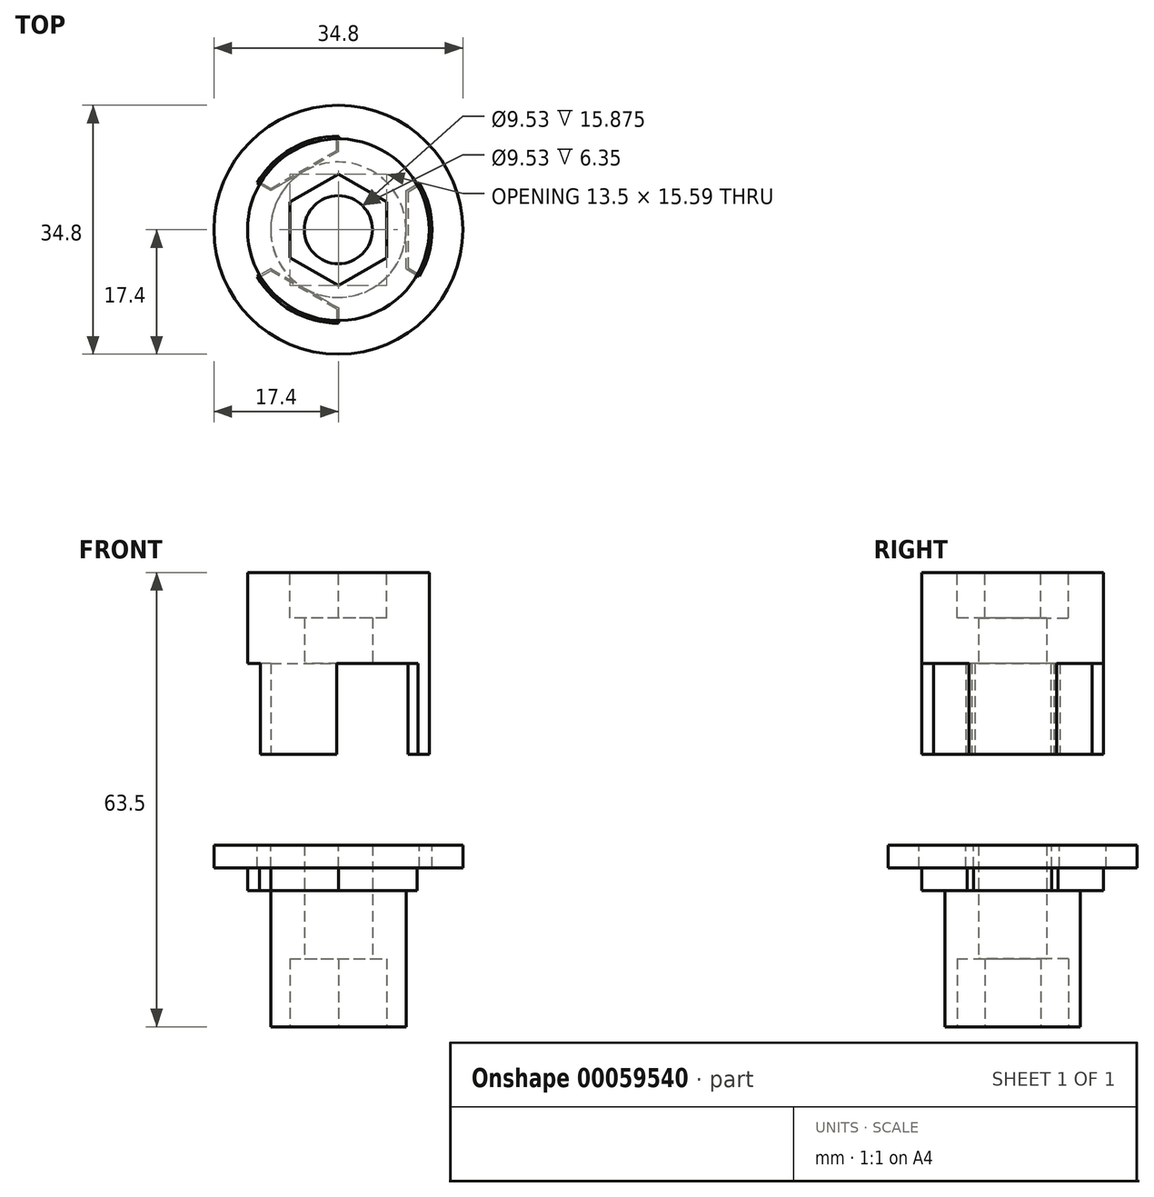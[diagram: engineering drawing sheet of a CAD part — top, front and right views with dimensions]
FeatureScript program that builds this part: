
annotation { "Feature Type Name" : "Feature", "Feature Type Description" : "" }
export const myFeature = defineFeature(function(context is Context, id is Id, definition is map)
    precondition{}
    {
        {
            var Q0;
            Q0=qCreatedBy(makeId("Front.planeOp"),FACE);
            var sketch = newSketch(context, id + "F0", { "sketchPlane" : qUnion([Q0])});
            skLineSegment(sketch, "E0", {"start": v(0, 0) * mm, "end": v(0, 20.45) * mm, "construction": true});
            skLineSegment(sketch, "E1", {"start": v(-4.76, 0) * mm, "end": v(-4.76, 6.35) * mm});
            skLineSegment(sketch, "E2", {"start": v(-4.76, 6.35) * mm, "end": v(-4.76, 6.35) * mm});
            skLineSegment(sketch, "E3", {"start": v(-4.76, 6.35) * mm, "end": v(-4.76, 25.4) * mm});
            skLineSegment(sketch, "E4", {"start": v(-4.76, 25.4) * mm, "end": v(-12.7, 25.4) * mm});
            skLineSegment(sketch, "E5", {"start": v(-12.7, 25.4) * mm, "end": v(-12.7, 19.05) * mm});
            skLineSegment(sketch, "E6", {"start": v(-12.7, 19.05) * mm, "end": v(-9.46, 19.05) * mm});
            skLineSegment(sketch, "E7", {"start": v(-9.46, 19.05) * mm, "end": v(-9.46, 0) * mm});
            skLineSegment(sketch, "E8", {"start": v(-9.46, 0) * mm, "end": v(-4.76, 0) * mm});
            skSolve(sketch);
        }
        {
            var Q0;
            Q0=makeQuery(id+"F0.imprint","IMPRINT",FACE,{"disambiguationData":[TD([[makeQuery(id+"F0.imprint","IMPRINT",EDGE,{"derivedFrom":sQuery(id+"F0.wireOp",EDGE,"E1")}),1.0]])]});
            var Q1;
            Q1=sQuery(id+"F0.wireOp",EDGE,"E0");
            revolve(context, id + "F1", {"entities" : qUnion([Q0]), "axis" : qUnion([Q1]), "revolveType" : RevolveType.FULL});
        }
        {
            var Q0;
            Q0=makeQuery(id+"F1.opRevolve","SWEPT_FACE",FACE,{"disambiguationData":[OSD([sQuery(id+"F0.wireOp",EDGE,"E8")])]});
            var sketch = newSketch(context, id + "F2", { "sketchPlane" : qUnion([Q0])});
            skCircle(sketch, "E9.cCircle", {"center": v(0, 0) * mm, "radius": 6.75 * mm, "construction": true});
            skLineSegment(sketch, "E9.0", {"start": v(6.75, 3.9) * mm, "end": v(6.75, -3.9) * mm});
            skLineSegment(sketch, "E9.1", {"start": v(6.75, -3.9) * mm, "end": v(0, -7.8) * mm});
            skLineSegment(sketch, "E9.2", {"start": v(0, -7.8) * mm, "end": v(-6.75, -3.9) * mm});
            skLineSegment(sketch, "E9.3", {"start": v(-6.75, -3.9) * mm, "end": v(-6.75, 3.9) * mm});
            skLineSegment(sketch, "E9.4", {"start": v(-6.75, 3.9) * mm, "end": v(0, 7.8) * mm});
            skLineSegment(sketch, "E9.5", {"start": v(0, 7.8) * mm, "end": v(6.75, 3.9) * mm});
            skPoint(sketch, "E9.0.midPoint", {"position": v(6.75, 0) * mm});
            skSolve(sketch);
        }
        {
            var Q0;
            Q0=makeQuery(id+"F2.imprint","IMPRINT",FACE,{"disambiguationData":[TD([[makeQuery(id+"F2.imprint","IMPRINT",EDGE,{"derivedFrom":sQuery(id+"F2.wireOp",EDGE,"E9.0")}),-1.0]])]});
            var Q1;
            Q1=makeQuery(id+"F1.opRevolve","SWEPT_FACE",FACE,{"disambiguationData":[OSD([sQuery(id+"F0.wireOp",EDGE,"E2")])]});
            extrude(context, id + "F3", {"entities" : qUnion([Q0]), "operationType" : NewBodyOperationType.REMOVE, "oppositeDirection" : true, "endBoundEntityFace" : qUnion([Q1]), "depth" : 9.52 * mm});
        }
        {
            var Q0;
            Q0=makeQuery(id+"F1.opRevolve","SWEPT_FACE",FACE,{"disambiguationData":[OSD([sQuery(id+"F0.wireOp",EDGE,"E4")])]});
            var sketch = newSketch(context, id + "F4", { "sketchPlane" : qUnion([Q0])});
            skLineSegment(sketch, "E10", {"start": v(0, 10.93) * mm, "end": v(0, 12.7) * mm});
            skLineSegment(sketch, "E11", {"start": v(0, 12.7) * mm, "end": v(-7.33, 12.7) * mm});
            skPoint(sketch, "E12.center", {"position": v(0, 0) * mm});
            skLineSegment(sketch, "E13", {"start": v(0, 0) * mm, "end": v(-7.33, 12.7) * mm, "construction": true});
            skLineSegment(sketch, "E14.MirrorCS", {"start": v(-11, 6.35) * mm, "end": v(-7.33, 12.7) * mm});
            skLineSegment(sketch, "E15.MirrorCS", {"start": v(-9.46, 5.46) * mm, "end": v(-11, 6.35) * mm});
            skLineSegment(sketch, "E16", {"start": v(0, 10.93) * mm, "end": v(-4.73, 8.2) * mm});
            skLineSegment(sketch, "E17.MirrorCS", {"start": v(-9.46, 16.39) * mm, "end": v(-2.13, 3.69) * mm, "construction": true});
            skLineSegment(sketch, "E18.MirrorCS", {"start": v(-9.46, 5.46) * mm, "end": v(-4.73, 8.2) * mm});
            skLineSegment(sketch, "E19.1.0", {"start": v(-9.46, -5.46) * mm, "end": v(-4.73, -8.2) * mm});
            skLineSegment(sketch, "E19.1.1", {"start": v(-11, -6.35) * mm, "end": v(-7.33, -12.7) * mm});
            skLineSegment(sketch, "E19.1.2", {"start": v(-9.46, -16.39) * mm, "end": v(-2.13, -3.69) * mm, "construction": true});
            skLineSegment(sketch, "E19.1.3", {"start": v(0, -10.93) * mm, "end": v(-4.73, -8.2) * mm});
            skLineSegment(sketch, "E19.1.4", {"start": v(0, -12.7) * mm, "end": v(-7.33, -12.7) * mm});
            skLineSegment(sketch, "E19.1.5", {"start": v(-9.46, -5.46) * mm, "end": v(-11, -6.35) * mm});
            skLineSegment(sketch, "E19.1.6", {"start": v(0, 0) * mm, "end": v(-7.33, -12.7) * mm, "construction": true});
            skLineSegment(sketch, "E19.1.7", {"start": v(0, -10.93) * mm, "end": v(0, -12.7) * mm});
            skLineSegment(sketch, "E19.2.0", {"start": v(9.46, -5.46) * mm, "end": v(9.46, 0) * mm});
            skLineSegment(sketch, "E19.2.1", {"start": v(11, -6.35) * mm, "end": v(14.66, 0) * mm});
            skLineSegment(sketch, "E19.2.2", {"start": v(18.92, 0) * mm, "end": v(4.26, 0) * mm, "construction": true});
            skLineSegment(sketch, "E19.2.3", {"start": v(9.46, 5.46) * mm, "end": v(9.46, 0) * mm});
            skLineSegment(sketch, "E19.2.4", {"start": v(11, 6.35) * mm, "end": v(14.66, 0) * mm});
            skLineSegment(sketch, "E19.2.5", {"start": v(9.46, -5.46) * mm, "end": v(11, -6.35) * mm});
            skLineSegment(sketch, "E19.2.6", {"start": v(0, 0) * mm, "end": v(14.66, 0) * mm, "construction": true});
            skLineSegment(sketch, "E19.2.7", {"start": v(9.46, 5.46) * mm, "end": v(11, 6.35) * mm});
            skSolve(sketch);
        }
        {
            var Q0;
            {var subQ1=sQuery(id+"F4.wireOp",EDGE,"E10");Q0=makeQuery(id+"F4.imprint","IMPRINT",FACE,{"disambiguationData":[TD([[makeQuery(id+"F4.imprint","IMPRINT",EDGE,{"derivedFrom":subQ1}),1.0]])]});}
            var Q1;
            Q1=makeQuery(id+"F4.imprint","IMPRINT",FACE,{"disambiguationData":[TD([[makeQuery(id+"F4.imprint","IMPRINT",EDGE,{"derivedFrom":sQuery(id+"F4.wireOp",EDGE,"E19.1.0")}),-1.0]])]});
            var Q2;
            Q2=makeQuery(id+"F4.imprint","IMPRINT",FACE,{"disambiguationData":[TD([[makeQuery(id+"F4.imprint","IMPRINT",EDGE,{"derivedFrom":sQuery(id+"F4.wireOp",EDGE,"E19.2.0")}),-1.0]])]});
            extrude(context, id + "F5", {"entities" : qUnion([Q0, Q1, Q2]), "operationType" : NewBodyOperationType.REMOVE, "oppositeDirection" : true, "depth" : 25.4 * mm});
        }
        {
            var Q0;
            Q0=makeQuery(id+"F1.opRevolve","SWEPT_FACE",FACE,{"disambiguationData":[OSD([sQuery(id+"F0.wireOp",EDGE,"E4")])]});
            cPlane(context, id + "F6", {"entities" : qUnion([Q0]), "cplaneType" : CPlaneType.OFFSET, "offset" : 12.7 * mm, "width" : 152.4 * mm, "height" : 152.4 * mm});
        }
        {
            var Q0;
            Q0=qCreatedBy(id+"F6.planeOp",FACE);
            var sketch = newSketch(context, id + "F7", { "sketchPlane" : qUnion([Q0])});
            skLineSegment(sketch, "E20.0", {"start": v(0, 11) * mm, "end": v(0, 12.7) * mm, "construction": true});
            skLineSegment(sketch, "E21.0", {"start": v(-0.25, 11.07) * mm, "end": v(-0.25, 12.7) * mm});
            skLineSegment(sketch, "E21.1", {"start": v(-9.46, 5.76) * mm, "end": v(-0.25, 11.07) * mm});
            skLineSegment(sketch, "E21.2", {"start": v(-9.46, 5.76) * mm, "end": v(-10.87, 6.57) * mm});
            skArc(sketch, "E22", {"start": v(-0.25, 12.7) * mm, "mid": v(-6.35, 11) * mm, "end": v(-10.87, 6.57) * mm});
            skLineSegment(sketch, "E23.0", {"start": v(-9.46, 5.46) * mm, "end": v(-11, 6.35) * mm, "construction": true});
            skLineSegment(sketch, "E24.0", {"start": v(0, 10.93) * mm, "end": v(-9.46, 5.46) * mm, "construction": true});
            skLineSegment(sketch, "E25.1.0", {"start": v(-9.46, -5.46) * mm, "end": v(0, -10.93) * mm, "construction": true});
            skLineSegment(sketch, "E25.1.1", {"start": v(-0.25, -11.07) * mm, "end": v(-0.25, -12.7) * mm});
            skLineSegment(sketch, "E25.1.2", {"start": v(-9.53, -5.5) * mm, "end": v(-11, -6.35) * mm, "construction": true});
            skLineSegment(sketch, "E25.1.3", {"start": v(0, -10.93) * mm, "end": v(0, -12.7) * mm, "construction": true});
            skLineSegment(sketch, "E25.1.4", {"start": v(-9.46, -5.76) * mm, "end": v(-10.87, -6.57) * mm});
            skLineSegment(sketch, "E25.1.5", {"start": v(-0.25, -11.07) * mm, "end": v(-9.46, -5.76) * mm});
            skArc(sketch, "E25.1.6", {"start": v(-10.87, -6.57) * mm, "mid": v(-6.35, -11) * mm, "end": v(-0.25, -12.7) * mm});
            skLineSegment(sketch, "E25.2.0", {"start": v(9.46, -5.46) * mm, "end": v(9.46, 5.46) * mm, "construction": true});
            skLineSegment(sketch, "E25.2.1", {"start": v(9.72, 5.32) * mm, "end": v(11.12, 6.13) * mm});
            skLineSegment(sketch, "E25.2.2", {"start": v(9.53, -5.5) * mm, "end": v(11, -6.35) * mm, "construction": true});
            skLineSegment(sketch, "E25.2.3", {"start": v(9.46, 5.46) * mm, "end": v(11, 6.35) * mm, "construction": true});
            skLineSegment(sketch, "E25.2.4", {"start": v(9.72, -5.32) * mm, "end": v(11.12, -6.13) * mm});
            skLineSegment(sketch, "E25.2.5", {"start": v(9.72, 5.32) * mm, "end": v(9.72, -5.32) * mm});
            skArc(sketch, "E25.2.6", {"start": v(11.12, -6.13) * mm, "mid": v(12.7, 0) * mm, "end": v(11.12, 6.13) * mm});
            skSolve(sketch);
        }
        {
            var Q0;
            Q0=makeQuery(id+"F7.imprint","IMPRINT",FACE,{"disambiguationData":[TD([[makeQuery(id+"F7.imprint","IMPRINT",EDGE,{"derivedFrom":sQuery(id+"F7.wireOp",EDGE,"E21.0")}),1.0]])]});
            var Q1;
            Q1=makeQuery(id+"F7.imprint","IMPRINT",FACE,{"disambiguationData":[TD([[makeQuery(id+"F7.imprint","IMPRINT",EDGE,{"derivedFrom":sQuery(id+"F7.wireOp",EDGE,"E25.2.1")}),-1.0]])]});
            var Q2;
            Q2=makeQuery(id+"F7.imprint","IMPRINT",FACE,{"disambiguationData":[TD([[makeQuery(id+"F7.imprint","IMPRINT",EDGE,{"derivedFrom":sQuery(id+"F7.wireOp",EDGE,"E25.1.1")}),-1.0]])]});
            extrude(context, id + "F8", {"entities" : qUnion([Q0, Q1, Q2]), "depth" : 12.7 * mm});
        }
        {
            var Q0;
            Q0=makeQuery(id+"F8.opExtrude","CAP_FACE",FACE,{"disambiguationData":[OSD([sQuery(id+"F7.wireOp",EDGE,"E21.0"),sQuery(id+"F7.wireOp",EDGE,"E21.1"),sQuery(id+"F7.wireOp",EDGE,"E21.2"),sQuery(id+"F7.wireOp",EDGE,"E22")])],"isStart":false});
            var sketch = newSketch(context, id + "F9", { "sketchPlane" : qUnion([Q0])});
            skCircle(sketch, "E26", {"center": v(0, 0) * mm, "radius": 12.7 * mm});
            skCircle(sketch, "E27.0", {"center": v(0, 0) * mm, "radius": 4.76 * mm});
            skSolve(sketch);
        }
        {
            var Q0;
            Q0=makeQuery(id+"F9.imprint","IMPRINT",FACE,{"disambiguationData":[TD([[makeQuery(id+"F9.imprint","IMPRINT",EDGE,{"derivedFrom":sQuery(id+"F9.wireOp",EDGE,"E27.0")}),-1.0]])]});
            var Q1;
            {var subQ1=makeQuery(id+"F8.opExtrude","CAP_EDGE",EDGE,{"disambiguationData":[OSD([sQuery(id+"F7.wireOp",EDGE,"E21.0")])],"isStart":false});Q1=makeQuery(id+"F9.imprint","IMPRINT",FACE,{"disambiguationData":[TD([[makeQuery(id+"F9.imprint","IMPRINT",EDGE,{"derivedFrom":subQ1}),1.0]])]});}
            extrude(context, id + "F10", {"entities" : qUnion([Q0, Q1]), "operationType" : NewBodyOperationType.ADD, "depth" : 12.7 * mm});
        }
        {
            var Q0;
            Q0=makeQuery(id+"F10.opExtrude","CAP_FACE",FACE,{"disambiguationData":[OSD([sQuery(id+"F9.wireOp",EDGE,"E26"),sQuery(id+"F9.wireOp",EDGE,"965c656a-fdfc-4771-a508-4816ac5dd99b")])],"isStart":false});
            var sketch = newSketch(context, id + "F11", { "sketchPlane" : qUnion([Q0])});
            skLineSegment(sketch, "E28.0", {"start": v(0, 7.8) * mm, "end": v(-6.75, 3.9) * mm});
            skLineSegment(sketch, "E29.0", {"start": v(6.75, 3.9) * mm, "end": v(0, 7.8) * mm});
            skLineSegment(sketch, "E30.0", {"start": v(6.75, -3.9) * mm, "end": v(6.75, 3.9) * mm});
            skLineSegment(sketch, "E31.0", {"start": v(0, -7.8) * mm, "end": v(6.75, -3.9) * mm});
            skLineSegment(sketch, "E32.0", {"start": v(-6.75, -3.9) * mm, "end": v(0, -7.8) * mm});
            skLineSegment(sketch, "E33.0", {"start": v(-6.75, 3.9) * mm, "end": v(-6.75, -3.9) * mm});
            skCircle(sketch, "E34.0", {"center": v(0, 0) * mm, "radius": 6.75 * mm, "construction": true});
            skSolve(sketch);
        }
        {
            var Q0;
            Q0=makeQuery(id+"F11.imprint","IMPRINT",FACE,{"disambiguationData":[TD([[makeQuery(id+"F11.imprint","IMPRINT",EDGE,{"derivedFrom":sQuery(id+"F11.wireOp",EDGE,"E28.0")}),1.0]])]});
            extrude(context, id + "F12", {"entities" : qUnion([Q0]), "operationType" : NewBodyOperationType.REMOVE, "oppositeDirection" : true, "depth" : 6.35 * mm});
        }
        {
            var Q0;
            Q0=makeQuery(id+"F1.opRevolve","SWEPT_FACE",FACE,{"disambiguationData":[OSD([sQuery(id+"F0.wireOp",EDGE,"E4")])]});
            var sketch = newSketch(context, id + "F13", { "sketchPlane" : qUnion([Q0])});
            skCircle(sketch, "E35", {"center": v(0, 0) * mm, "radius": 17.4 * mm});
            skArc(sketch, "E36.0", {"start": v(11.33, -6.54) * mm, "mid": v(13.08, 0) * mm, "end": v(11.33, 6.54) * mm});
            skArc(sketch, "E37.0", {"start": v(0, -12.7) * mm, "mid": v(6.35, -11) * mm, "end": v(11, -6.35) * mm});
            skLineSegment(sketch, "E38", {"start": v(0, -12.7) * mm, "end": v(0, -13.08) * mm});
            skLineSegment(sketch, "E39", {"start": v(-11, -6.35) * mm, "end": v(-11.33, -6.54) * mm});
            skLineSegment(sketch, "E40", {"start": v(11, -6.35) * mm, "end": v(11.33, -6.54) * mm});
            skLineSegment(sketch, "E41", {"start": v(11, 6.35) * mm, "end": v(11.33, 6.54) * mm});
            skArc(sketch, "E42.trimOffspring", {"start": v(11, 6.35) * mm, "mid": v(6.35, 11) * mm, "end": v(0, 12.7) * mm});
            skLineSegment(sketch, "E43", {"start": v(0, 12.7) * mm, "end": v(0, 13.08) * mm});
            skLineSegment(sketch, "E44", {"start": v(-11, 6.35) * mm, "end": v(-11.33, 6.54) * mm});
            skArc(sketch, "E45.trimOffspring", {"start": v(-11, 6.35) * mm, "mid": v(-12.7, 0) * mm, "end": v(-11, -6.35) * mm});
            skArc(sketch, "E46.trimOffspring", {"start": v(-11.33, -6.54) * mm, "mid": v(-6.54, -11.33) * mm, "end": v(0, -13.08) * mm});
            skArc(sketch, "E47.trimOffspring", {"start": v(0, 13.08) * mm, "mid": v(-6.54, 11.33) * mm, "end": v(-11.33, 6.54) * mm});
            skSolve(sketch);
        }
        {
            var Q0;
            Q0=makeQuery(id+"F13.imprint","IMPRINT",FACE,{"disambiguationData":[TD([[makeQuery(id+"F13.imprint","IMPRINT",EDGE,{"derivedFrom":sQuery(id+"F13.wireOp",EDGE,"E35")}),1.0]])]});
            extrude(context, id + "F14", {"entities" : qUnion([Q0]), "operationType" : NewBodyOperationType.ADD, "oppositeDirection" : true, "depth" : 3.17 * mm});
        }
    });
